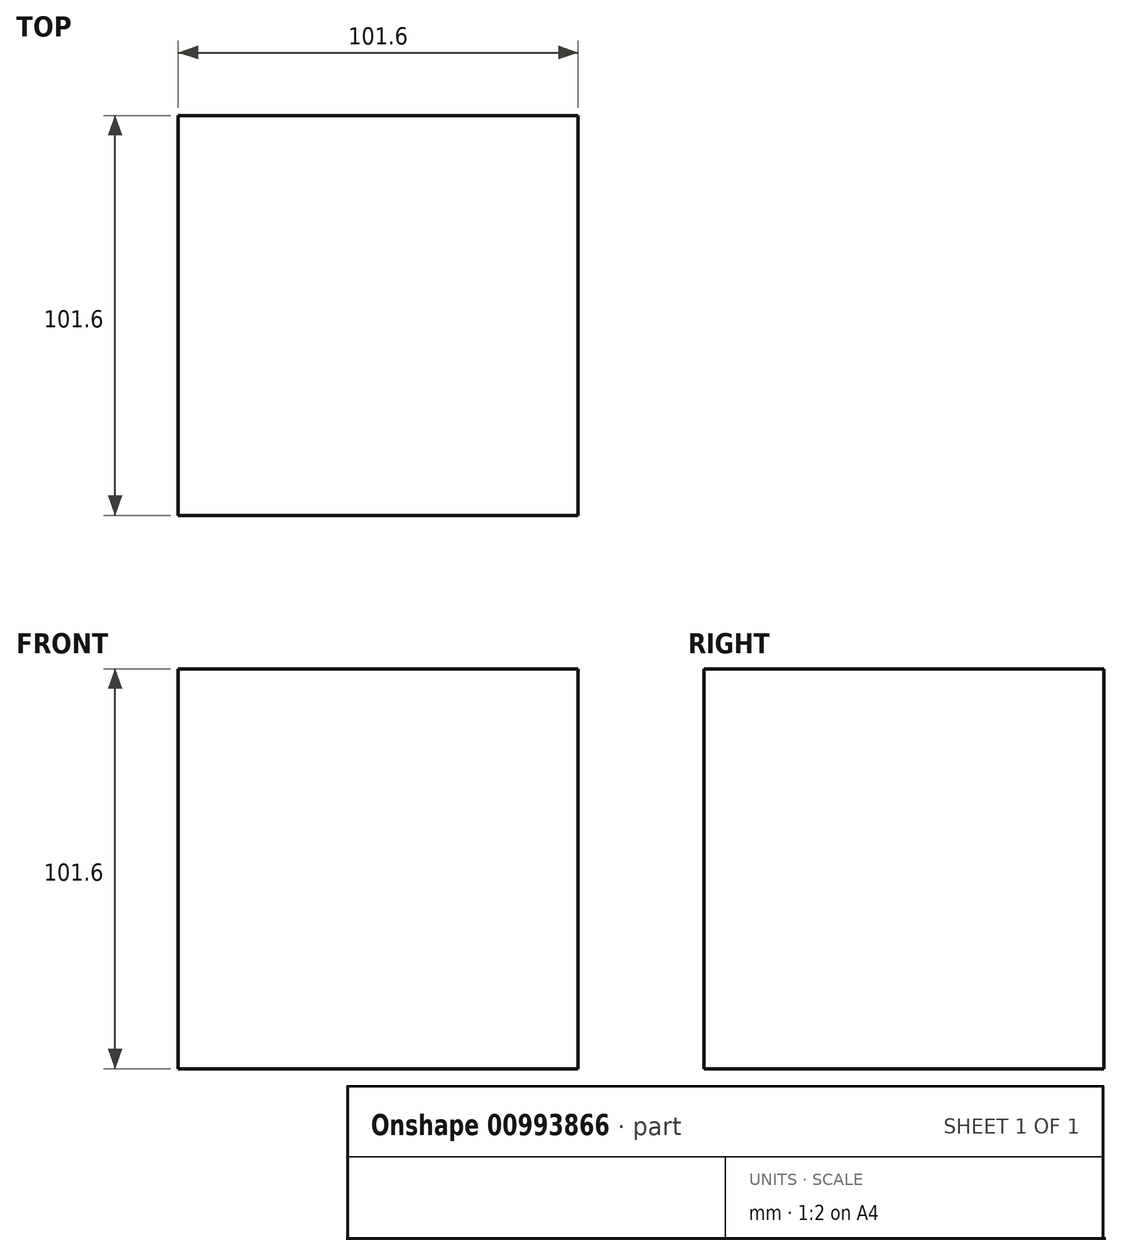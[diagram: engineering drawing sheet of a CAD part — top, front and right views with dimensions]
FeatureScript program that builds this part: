
annotation { "Feature Type Name" : "Feature", "Feature Type Description" : "" }
export const myFeature = defineFeature(function(context is Context, id is Id, definition is map)
    precondition{}
    {
        {
            var Q0;
            Q0=qCreatedBy(makeId("Top.planeOp"),FACE);
            var sketch = newSketch(context, id + "F0", { "sketchPlane" : qUnion([Q0])});
            skLineSegment(sketch, "E0.bottom", {"start": v(-50.8, -50.8) * mm, "end": v(50.8, -50.8) * mm});
            skLineSegment(sketch, "E0.top", {"start": v(-50.8, 50.8) * mm, "end": v(50.8, 50.8) * mm});
            skLineSegment(sketch, "E0.left", {"start": v(-50.8, -50.8) * mm, "end": v(-50.8, 50.8) * mm});
            skLineSegment(sketch, "E0.right", {"start": v(50.8, -50.8) * mm, "end": v(50.8, 50.8) * mm});
            skPoint(sketch, "E0.middle", {"position": v(0, 0) * mm});
            skSolve(sketch);
        }
        {
            var Q0;
            Q0=makeQuery(id+"F0.imprint","IMPRINT",FACE,{"disambiguationData":[TD([[makeQuery(id+"F0.imprint","IMPRINT",EDGE,{"derivedFrom":sQuery(id+"F0.wireOp",EDGE,"E0.bottom")}),1.0]])]});
            extrude(context, id + "F1", {"entities" : qUnion([Q0]), "depth" : 101.6 * mm, "offsetDistance" : 25 * mm});
        }
    });
